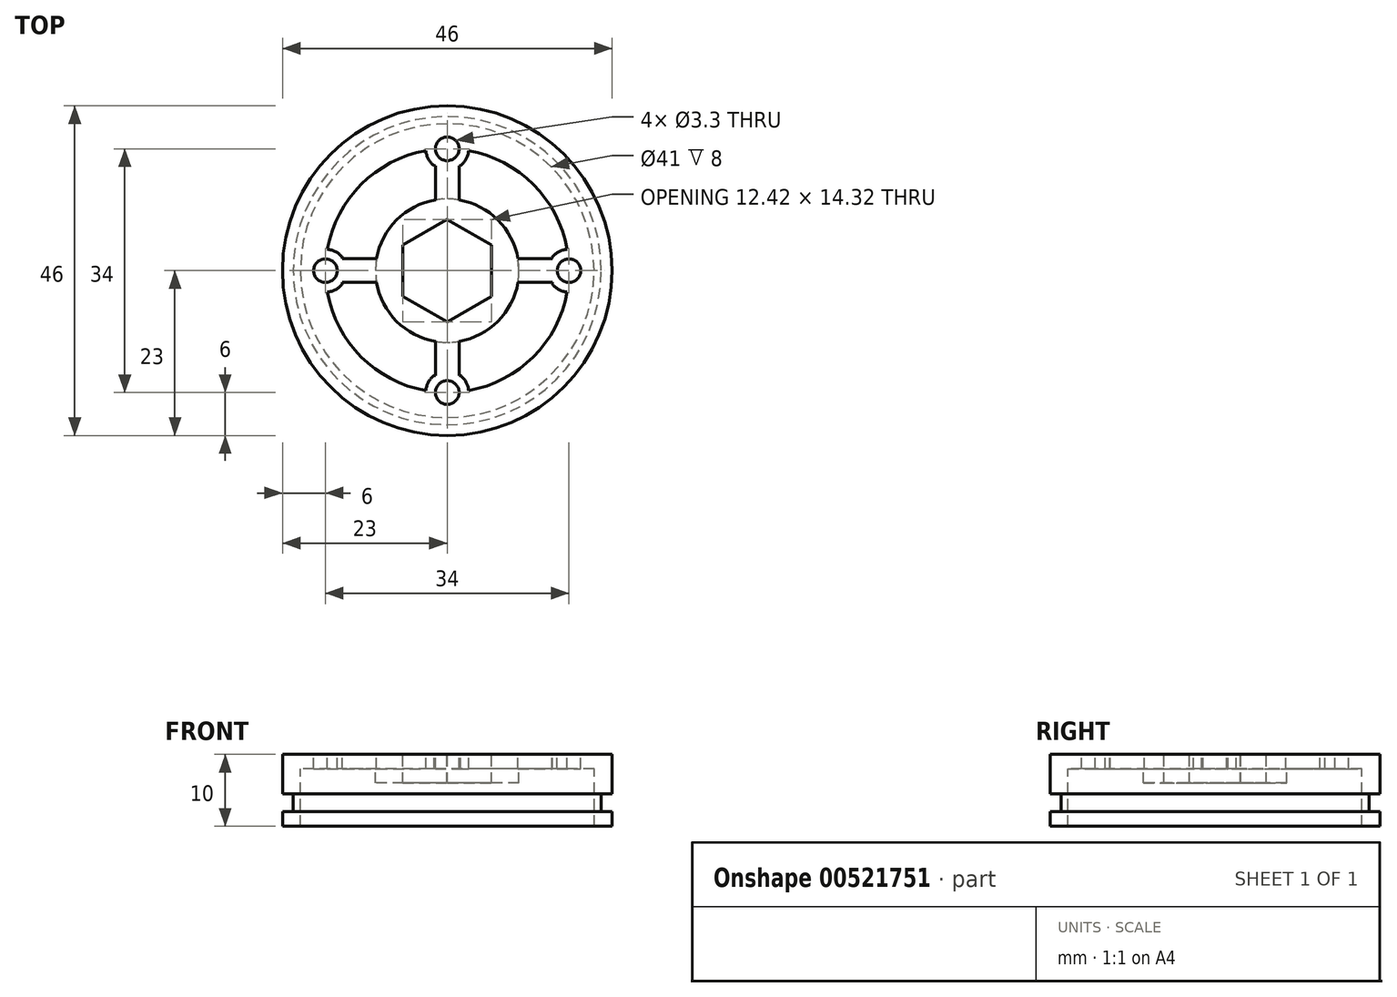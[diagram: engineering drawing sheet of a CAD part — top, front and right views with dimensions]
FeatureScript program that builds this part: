
annotation { "Feature Type Name" : "Feature", "Feature Type Description" : "" }
export const myFeature = defineFeature(function(context is Context, id is Id, definition is map)
    precondition{}
    {
        {
            var Q0;
            Q0=qCreatedBy(makeId("Front.planeOp"),FACE);
            var sketch = newSketch(context, id + "F0", { "sketchPlane" : qUnion([Q0])});
            skLineSegment(sketch, "E0", {"start": v(0, 18.35) * mm, "end": v(0, 16.35) * mm});
            skLineSegment(sketch, "E1", {"start": v(20.5, 8.35) * mm, "end": v(23, 8.35) * mm});
            skLineSegment(sketch, "E2", {"start": v(23, 8.35) * mm, "end": v(23, 10.35) * mm});
            skLineSegment(sketch, "E3", {"start": v(23, 10.35) * mm, "end": v(21.5, 10.35) * mm});
            skLineSegment(sketch, "E4", {"start": v(21.5, 10.35) * mm, "end": v(21.5, 12.85) * mm});
            skLineSegment(sketch, "E5", {"start": v(21.5, 12.85) * mm, "end": v(23, 12.85) * mm});
            skLineSegment(sketch, "E6", {"start": v(23, 12.85) * mm, "end": v(23, 18.35) * mm});
            skLineSegment(sketch, "E7", {"start": v(23, 18.35) * mm, "end": v(14.75, 18.35) * mm});
            skLineSegment(sketch, "E8", {"start": v(20.5, 8.35) * mm, "end": v(20.5, 16.35) * mm});
            skLineSegment(sketch, "E9", {"start": v(20.5, 16.35) * mm, "end": v(14.75, 16.35) * mm});
            skLineSegment(sketch, "E10", {"start": v(14.75, 18.35) * mm, "end": v(14.75, 16.35) * mm});
            skSolve(sketch);
        }
        {
            var Q0;
            Q0=makeQuery(id+"F0.imprint","IMPRINT",FACE,{"disambiguationData":[TD([[makeQuery(id+"F0.imprint","IMPRINT",EDGE,{"derivedFrom":sQuery(id+"F0.wireOp",EDGE,"E1")}),1.0]])]});
            var Q1;
            Q1=sQuery(id+"F0.wireOp",EDGE,"E0");
            revolve(context, id + "F1", {"entities" : qUnion([Q0]), "axis" : qUnion([Q1]), "revolveType" : RevolveType.FULL});
        }
        {
            var Q0;
            Q0=makeQuery(id+"F1.opRevolve","SWEPT_FACE",FACE,{"disambiguationData":[OSD([sQuery(id+"F0.wireOp",EDGE,"E7")])]});
            var sketch = newSketch(context, id + "F2", { "sketchPlane" : qUnion([Q0])});
            skCircle(sketch, "E11", {"center": v(0, 17) * mm, "radius": 1.65 * mm});
            skCircle(sketch, "E12", {"center": v(0, -17) * mm, "radius": 1.65 * mm});
            skCircle(sketch, "E13", {"center": v(17, 0) * mm, "radius": 1.65 * mm});
            skCircle(sketch, "E14", {"center": v(-17, 0) * mm, "radius": 1.65 * mm});
            skSolve(sketch);
        }
        {
            var Q0;
            Q0=makeQuery(id+"F2.imprint","IMPRINT",FACE,{"disambiguationData":[TD([[makeQuery(id+"F2.imprint","IMPRINT",EDGE,{"derivedFrom":sQuery(id+"F2.wireOp",EDGE,"E11")}),1.0]])]});
            var Q1;
            Q1=makeQuery(id+"F2.imprint","IMPRINT",FACE,{"disambiguationData":[TD([[makeQuery(id+"F2.imprint","IMPRINT",EDGE,{"derivedFrom":sQuery(id+"F2.wireOp",EDGE,"E13")}),1.0]])]});
            var Q2;
            Q2=makeQuery(id+"F2.imprint","IMPRINT",FACE,{"disambiguationData":[TD([[makeQuery(id+"F2.imprint","IMPRINT",EDGE,{"derivedFrom":sQuery(id+"F2.wireOp",EDGE,"E14")}),1.0]])]});
            var Q3;
            Q3=makeQuery(id+"F2.imprint","IMPRINT",FACE,{"disambiguationData":[TD([[makeQuery(id+"F2.imprint","IMPRINT",EDGE,{"derivedFrom":sQuery(id+"F2.wireOp",EDGE,"E12")}),1.0]])]});
            extrude(context, id + "F3", {"entities" : qUnion([Q0, Q1, Q2, Q3]), "operationType" : NewBodyOperationType.REMOVE, "endBound" : BoundingType.THROUGH_ALL, "oppositeDirection" : true, "depth" : 25 * mm, "offsetDistance" : 25 * mm});
        }
        {
            var Q0;
            Q0=makeQuery(id+"F1.opRevolve","SWEPT_FACE",FACE,{"disambiguationData":[OSD([sQuery(id+"F0.wireOp",EDGE,"E7")])]});
            var sketch = newSketch(context, id + "F4", { "sketchPlane" : qUnion([Q0])});
            skArc(sketch, "E15", {"start": v(-1.65, 9.86) * mm, "mid": v(-7.07, 7.07) * mm, "end": v(-9.86, 1.65) * mm});
            skLineSegment(sketch, "E16", {"start": v(-17.07, 1.65) * mm, "end": v(-9.86, 1.65) * mm});
            skLineSegment(sketch, "E17", {"start": v(17, -1.65) * mm, "end": v(9.86, -1.65) * mm});
            skLineSegment(sketch, "E18", {"start": v(1.65, 16.99) * mm, "end": v(1.65, 9.86) * mm});
            skLineSegment(sketch, "E19", {"start": v(-1.65, -17) * mm, "end": v(-1.65, -9.86) * mm});
            skLineSegment(sketch, "E20.trimOffspring", {"start": v(9.86, 1.65) * mm, "end": v(17, 1.65) * mm});
            skLineSegment(sketch, "E21.trimOffspring", {"start": v(-1.65, 9.86) * mm, "end": v(-1.65, 16.99) * mm});
            skLineSegment(sketch, "E22.trimOffspring", {"start": v(1.65, -9.86) * mm, "end": v(1.65, -17) * mm});
            skArc(sketch, "E23.trimOffspring", {"start": v(9.86, 1.65) * mm, "mid": v(7.07, 7.07) * mm, "end": v(1.65, 9.86) * mm});
            skLineSegment(sketch, "E24.trimOffspring", {"start": v(-9.86, -1.65) * mm, "end": v(-17, -1.65) * mm});
            skArc(sketch, "E25.trimOffspring", {"start": v(1.65, -9.86) * mm, "mid": v(7.07, -7.07) * mm, "end": v(9.86, -1.65) * mm});
            skArc(sketch, "E26.trimOffspring", {"start": v(-9.86, -1.65) * mm, "mid": v(-7.07, -7.07) * mm, "end": v(-1.65, -9.86) * mm});
            skSolve(sketch);
        }
        {
            var Q0;
            {var subQ5=sQuery(id+"F4.wireOp",EDGE,"E15");Q0=makeQuery(id+"F4.imprint","IMPRINT",FACE,{"disambiguationData":[TD([[makeQuery(id+"F4.imprint","IMPRINT",EDGE,{"derivedFrom":subQ5}),1.0]])]});}
            var Q1;
            {var subQ0=sQuery(id+"F4.wireOp",EDGE,"E18");var subQ1=makeQuery(id+"F3.boolean.opBoolean","COPY",EDGE,{"derivedFrom":makeQuery(id+"F3.opExtrude","CAP_EDGE",EDGE,{"disambiguationData":[OSD([sQuery(id+"F2.wireOp",EDGE,"E11")])],"isStart":true})});var subQ2=makeQuery(id+"F4.imprint","INTERSECT",VERTEX,{"derivedFrom":[subQ1,subQ0]});Q1=makeQuery(id+"F4.imprint","IMPRINT",FACE,{"disambiguationData":[TD([[makeQuery(id+"F4.imprint","IMPRINT",EDGE,{"disambiguationData":[TD([[subQ2,1.0]])],"derivedFrom":subQ1}),-1.0]])]});}
            var Q2;
            {var subQ0=sQuery(id+"F4.wireOp",EDGE,"E17");var subQ1=makeQuery(id+"F3.boolean.opBoolean","COPY",EDGE,{"derivedFrom":makeQuery(id+"F3.opExtrude","CAP_EDGE",EDGE,{"disambiguationData":[OSD([sQuery(id+"F2.wireOp",EDGE,"E13")])],"isStart":true})});var subQ2=makeQuery(id+"F4.imprint","INTERSECT",VERTEX,{"derivedFrom":[subQ1,subQ0]});Q2=makeQuery(id+"F4.imprint","IMPRINT",FACE,{"disambiguationData":[TD([[makeQuery(id+"F4.imprint","IMPRINT",EDGE,{"disambiguationData":[TD([[subQ2,1.0]])],"derivedFrom":subQ1}),-1.0]])]});}
            var Q3;
            {var subQ1=makeQuery(id+"F3.boolean.opBoolean","COPY",EDGE,{"derivedFrom":makeQuery(id+"F3.opExtrude","CAP_EDGE",EDGE,{"disambiguationData":[OSD([sQuery(id+"F2.wireOp",EDGE,"E14")])],"isStart":true})});var subQ5=sQuery(id+"F4.wireOp",EDGE,"E24.trimOffspring");var subQ6=makeQuery(id+"F4.imprint","INTERSECT",VERTEX,{"derivedFrom":[subQ1,subQ5]});Q3=makeQuery(id+"F4.imprint","IMPRINT",FACE,{"disambiguationData":[TD([[makeQuery(id+"F4.imprint","IMPRINT",EDGE,{"disambiguationData":[TD([[subQ6,-1.0]])],"derivedFrom":subQ1}),-1.0]])]});}
            var Q4;
            {var subQ0=sQuery(id+"F4.wireOp",EDGE,"E19");var subQ1=makeQuery(id+"F3.boolean.opBoolean","COPY",EDGE,{"derivedFrom":makeQuery(id+"F3.opExtrude","CAP_EDGE",EDGE,{"disambiguationData":[OSD([sQuery(id+"F2.wireOp",EDGE,"E12")])],"isStart":true})});var subQ2=makeQuery(id+"F4.imprint","INTERSECT",VERTEX,{"derivedFrom":[subQ1,subQ0]});Q4=makeQuery(id+"F4.imprint","IMPRINT",FACE,{"disambiguationData":[TD([[makeQuery(id+"F4.imprint","IMPRINT",EDGE,{"disambiguationData":[TD([[subQ2,1.0]])],"derivedFrom":subQ1}),-1.0]])]});}
            extrude(context, id + "F5", {"entities" : qUnion([Q0, Q1, Q2, Q3, Q4]), "operationType" : NewBodyOperationType.ADD, "oppositeDirection" : true, "depth" : 2 * mm, "offsetDistance" : 25 * mm});
        }
        {
            var Q0;
            Q0=makeQuery(id+"F5.boolean.opBoolean","MERGE",FACE,{"derivedFrom":[makeQuery(id+"F1.opRevolve","SWEPT_FACE",FACE,{"disambiguationData":[OSD([sQuery(id+"F0.wireOp",EDGE,"E7")])]}),makeQuery(id+"F5.opExtrude","CAP_FACE",FACE,{"disambiguationData":[OSD([sQuery(id+"F2.wireOp",EDGE,"E11"),sQuery(id+"F2.wireOp",EDGE,"E12"),sQuery(id+"F2.wireOp",EDGE,"E13"),sQuery(id+"F2.wireOp",EDGE,"E14"),sQuery(id+"F4.wireOp",EDGE,"E15"),sQuery(id+"F4.wireOp",EDGE,"E16"),sQuery(id+"F4.wireOp",EDGE,"E17"),sQuery(id+"F4.wireOp",EDGE,"E18"),sQuery(id+"F4.wireOp",EDGE,"E19"),sQuery(id+"F4.wireOp",EDGE,"E20.trimOffspring"),sQuery(id+"F4.wireOp",EDGE,"E21.trimOffspring"),sQuery(id+"F4.wireOp",EDGE,"E22.trimOffspring"),sQuery(id+"F4.wireOp",EDGE,"E23.trimOffspring"),sQuery(id+"F4.wireOp",EDGE,"E24.trimOffspring"),sQuery(id+"F4.wireOp",EDGE,"E25.trimOffspring"),sQuery(id+"F4.wireOp",EDGE,"E26.trimOffspring")])],"isStart":true})]});
            var sketch = newSketch(context, id + "F6", { "sketchPlane" : qUnion([Q0])});
            skArc(sketch, "E27", {"start": v(-2.99, 16.74) * mm, "mid": v(-12.02, 12.02) * mm, "end": v(-16.74, 2.99) * mm});
            skArc(sketch, "E28", {"start": v(-2.99, 16.74) * mm, "mid": v(0, 14) * mm, "end": v(2.99, 16.74) * mm});
            skArc(sketch, "E29", {"start": v(16.74, 2.99) * mm, "mid": v(14, 0) * mm, "end": v(16.74, -2.99) * mm});
            skArc(sketch, "E30", {"start": v(-16.74, -2.99) * mm, "mid": v(-14, 0) * mm, "end": v(-16.74, 2.99) * mm});
            skArc(sketch, "E31", {"start": v(2.99, -16.74) * mm, "mid": v(0, -14) * mm, "end": v(-2.99, -16.74) * mm});
            skCircle(sketch, "E32.cCircle", {"center": v(0, 0) * mm, "radius": 6.2 * mm, "construction": true});
            skLineSegment(sketch, "E32.0", {"start": v(6.2, -3.56) * mm, "end": v(0.02, -7.16) * mm});
            skLineSegment(sketch, "E32.1", {"start": v(0.02, -7.16) * mm, "end": v(-6.2, -3.6) * mm});
            skLineSegment(sketch, "E32.2", {"start": v(-6.2, -3.6) * mm, "end": v(-6.2, 3.56) * mm});
            skLineSegment(sketch, "E32.3", {"start": v(-6.2, 3.56) * mm, "end": v(-0.02, 7.16) * mm});
            skLineSegment(sketch, "E32.4", {"start": v(-0.02, 7.16) * mm, "end": v(6.2, 3.6) * mm});
            skLineSegment(sketch, "E32.5", {"start": v(6.2, 3.6) * mm, "end": v(6.2, -3.56) * mm});
            skPoint(sketch, "E32.0.midPoint", {"position": v(3.11, -5.36) * mm});
            skArc(sketch, "E33.trimOffspring", {"start": v(-16.74, -2.99) * mm, "mid": v(-12.02, -12.02) * mm, "end": v(-2.99, -16.74) * mm});
            skArc(sketch, "E34.trimOffspring", {"start": v(2.99, -16.74) * mm, "mid": v(12.02, -12.02) * mm, "end": v(16.74, -2.99) * mm});
            skArc(sketch, "E35.trimOffspring", {"start": v(16.74, 2.99) * mm, "mid": v(12.02, 12.02) * mm, "end": v(2.99, 16.74) * mm});
            skSolve(sketch);
        }
        {
            var Q0;
            {var subQ0=sQuery(id+"F6.wireOp",EDGE,"E27");Q0=makeQuery(id+"F6.imprint","IMPRINT",FACE,{"disambiguationData":[TD([[makeQuery(id+"F6.imprint","IMPRINT",EDGE,{"derivedFrom":subQ0}),1.0]])]});}
            var Q1;
            {var subQ0=sQuery(id+"F6.wireOp",EDGE,"E35.trimOffspring");Q1=makeQuery(id+"F6.imprint","IMPRINT",FACE,{"disambiguationData":[TD([[makeQuery(id+"F6.imprint","IMPRINT",EDGE,{"derivedFrom":subQ0}),1.0]])]});}
            var Q2;
            {var subQ0=sQuery(id+"F6.wireOp",EDGE,"E34.trimOffspring");Q2=makeQuery(id+"F6.imprint","IMPRINT",FACE,{"disambiguationData":[TD([[makeQuery(id+"F6.imprint","IMPRINT",EDGE,{"derivedFrom":subQ0}),1.0]])]});}
            var Q3;
            {var subQ0=sQuery(id+"F6.wireOp",EDGE,"E33.trimOffspring");Q3=makeQuery(id+"F6.imprint","IMPRINT",FACE,{"disambiguationData":[TD([[makeQuery(id+"F6.imprint","IMPRINT",EDGE,{"derivedFrom":subQ0}),1.0]])]});}
            var Q4;
            Q4=makeQuery(id+"F6.imprint","IMPRINT",FACE,{"disambiguationData":[TD([[makeQuery(id+"F6.imprint","IMPRINT",EDGE,{"derivedFrom":sQuery(id+"F6.wireOp",EDGE,"E32.0")}),-1.0]])]});
            extrude(context, id + "F7", {"entities" : qUnion([Q0, Q1, Q2, Q3, Q4]), "operationType" : NewBodyOperationType.REMOVE, "endBound" : BoundingType.THROUGH_ALL, "oppositeDirection" : true, "depth" : 25 * mm, "offsetDistance" : 25 * mm});
        }
        {
            var Q0;
            Q0=makeQuery(id+"F5.boolean.opBoolean","MERGE",FACE,{"derivedFrom":[makeQuery(id+"F1.opRevolve","SWEPT_FACE",FACE,{"disambiguationData":[OSD([sQuery(id+"F0.wireOp",EDGE,"E9")])]}),makeQuery(id+"F5.opExtrude","CAP_FACE",FACE,{"disambiguationData":[OSD([sQuery(id+"F2.wireOp",EDGE,"E11"),sQuery(id+"F2.wireOp",EDGE,"E12"),sQuery(id+"F2.wireOp",EDGE,"E13"),sQuery(id+"F2.wireOp",EDGE,"E14"),sQuery(id+"F4.wireOp",EDGE,"E15"),sQuery(id+"F4.wireOp",EDGE,"E16"),sQuery(id+"F4.wireOp",EDGE,"E17"),sQuery(id+"F4.wireOp",EDGE,"E18"),sQuery(id+"F4.wireOp",EDGE,"E19"),sQuery(id+"F4.wireOp",EDGE,"E20.trimOffspring"),sQuery(id+"F4.wireOp",EDGE,"E21.trimOffspring"),sQuery(id+"F4.wireOp",EDGE,"E22.trimOffspring"),sQuery(id+"F4.wireOp",EDGE,"E23.trimOffspring"),sQuery(id+"F4.wireOp",EDGE,"E24.trimOffspring"),sQuery(id+"F4.wireOp",EDGE,"E25.trimOffspring"),sQuery(id+"F4.wireOp",EDGE,"E26.trimOffspring")])],"isStart":false})]});
            var sketch = newSketch(context, id + "F8", { "sketchPlane" : qUnion([Q0])});
            skCircle(sketch, "E36", {"center": v(0, 0) * mm, "radius": 10 * mm});
            skSolve(sketch);
        }
        {
            var Q0;
            {var subQ3=sQuery(id+"F4.wireOp",EDGE,"E20.trimOffspring");var subQ5=sQuery(id+"F4.wireOp",EDGE,"E18");var subQ9=sQuery(id+"F8.wireOp",EDGE,"E36");var subQ11=makeQuery(id+"F8.imprint","INTERSECT",VERTEX,{"derivedFrom":[makeQuery(id+"F5.opExtrude","CAP_EDGE",EDGE,{"disambiguationData":[OSD([subQ3])],"isStart":false}),subQ9]});var subQ13=makeQuery(id+"F8.imprint","INTERSECT",VERTEX,{"derivedFrom":[makeQuery(id+"F5.opExtrude","CAP_EDGE",EDGE,{"disambiguationData":[OSD([subQ5])],"isStart":false}),subQ9]});Q0=makeQuery(id+"F8.imprint","IMPRINT",FACE,{"disambiguationData":[TD([[makeQuery(id+"F8.imprint","IMPRINT",EDGE,{"disambiguationData":[TD([[subQ13,1.0],[subQ11,-1.0]])],"derivedFrom":subQ9}),-1.0]])]});}
            extrude(context, id + "F9", {"entities" : qUnion([Q0]), "operationType" : NewBodyOperationType.ADD, "depth" : 2 * mm, "offsetDistance" : 25 * mm});
        }
    });
